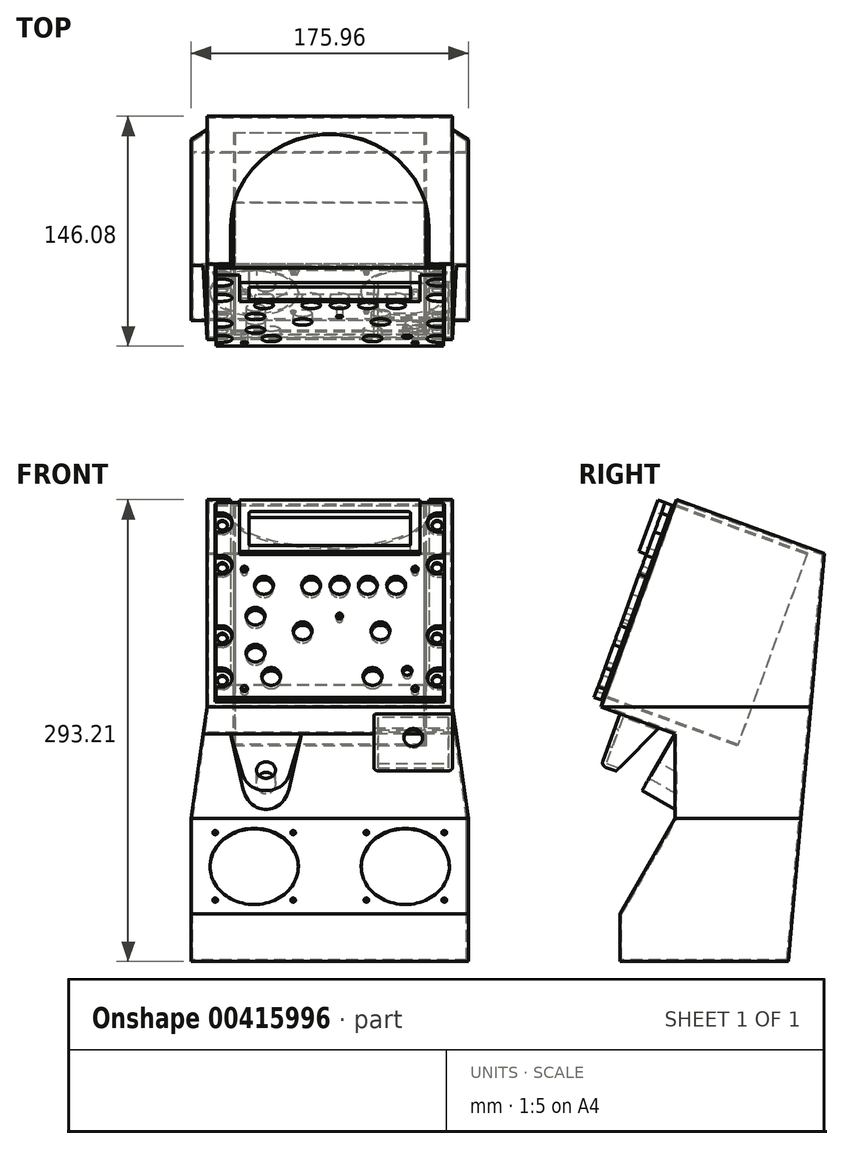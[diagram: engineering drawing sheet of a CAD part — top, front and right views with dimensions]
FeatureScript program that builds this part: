
annotation { "Feature Type Name" : "Feature", "Feature Type Description" : "" }
export const myFeature = defineFeature(function(context is Context, id is Id, definition is map)
    precondition{}
    {
        {
            var Q0;
            Q0=qCreatedBy(makeId("Right.planeOp"),FACE);
            var sketch = newSketch(context, id + "F0", { "sketchPlane" : qUnion([Q0])});
            skLineSegment(sketch, "E0", {"start": v(0, 0) * mm, "end": v(-47.88, -131.56) * mm});
            skLineSegment(sketch, "E1", {"start": v(-47.88, -131.56) * mm, "end": v(-0.9, -148.66) * mm});
            skLineSegment(sketch, "E2", {"start": v(-0.9, -148.66) * mm, "end": v(-0.9, -202.6) * mm});
            skLineSegment(sketch, "E3", {"start": v(-0.9, -202.6) * mm, "end": v(-35.9, -263.21) * mm});
            skLineSegment(sketch, "E4", {"start": v(-35.9, -263.21) * mm, "end": v(-35.9, -293.21) * mm});
            skLineSegment(sketch, "E5", {"start": v(-35.9, -293.21) * mm, "end": v(71.3, -293.21) * mm});
            skLineSegment(sketch, "E6", {"start": v(71.3, -293.21) * mm, "end": v(93.97, -34.2) * mm});
            skLineSegment(sketch, "E7", {"start": v(93.97, -34.2) * mm, "end": v(0, 0) * mm});
            skSolve(sketch);
        }
        {
            var Q0;
            Q0=qSketchRegion(id+"F0",true);
            extrude(context, id + "F1", {"entities" : qUnion([Q0]), "depth" : 200 * mm});
        }
        {
            var Q0;
            Q0=makeQuery(id+"F1.opExtrude","SWEPT_FACE",FACE,{"disambiguationData":[OSD([sQuery(id+"F0.wireOp",EDGE,"E2")])]});
            var sketch = newSketch(context, id + "F2", { "sketchPlane" : qUnion([Q0])});
            skLineSegment(sketch, "E8", {"start": v(178, 0) * mm, "end": v(178, -131.56) * mm});
            skLineSegment(sketch, "E9", {"start": v(178, -131.56) * mm, "end": v(187.98, -202.6) * mm});
            skLineSegment(sketch, "E10", {"start": v(187.98, -202.6) * mm, "end": v(187.98, -293.21) * mm});
            skLineSegment(sketch, "E11", {"start": v(187.98, -293.21) * mm, "end": v(228, -293.21) * mm});
            skLineSegment(sketch, "E12", {"start": v(228, -293.21) * mm, "end": v(228, 0) * mm});
            skLineSegment(sketch, "E13", {"start": v(228, 0) * mm, "end": v(178, 0) * mm});
            skLineSegment(sketch, "E14", {"start": v(0, 0) * mm, "end": v(22, 0) * mm});
            skLineSegment(sketch, "E15", {"start": v(22, 0) * mm, "end": v(22, -131.56) * mm});
            skLineSegment(sketch, "E16", {"start": v(22, -131.56) * mm, "end": v(12.02, -202.6) * mm});
            skLineSegment(sketch, "E17", {"start": v(12.02, -202.6) * mm, "end": v(12.02, -293.21) * mm});
            skLineSegment(sketch, "E18", {"start": v(12.02, -293.21) * mm, "end": v(-28, -293.21) * mm});
            skLineSegment(sketch, "E19", {"start": v(-28, -293.21) * mm, "end": v(-28, 0) * mm});
            skLineSegment(sketch, "E20", {"start": v(-28, 0) * mm, "end": v(22, 0) * mm});
            skLineSegment(sketch, "E21", {"start": v(22, -35.34) * mm, "end": v(0, -35.34) * mm, "construction": true});
            skLineSegment(sketch, "E22", {"start": v(178, -36.32) * mm, "end": v(200, -36.32) * mm, "construction": true});
            skSolve(sketch);
        }
        {
            var Q0;
            Q0=qSketchRegion(id+"F2",true);
            var Q1;
            Q1=makeQuery(id+"F1.opExtrude","SWEPT_FACE",FACE,{"disambiguationData":[OSD([sQuery(id+"F0.wireOp",EDGE,"E6")])]});
            extrude(context, id + "F3", {"entities" : qUnion([Q0]), "operationType" : NewBodyOperationType.REMOVE, "endBound" : BoundingType.UP_TO_SURFACE, "oppositeDirection" : true, "endBoundEntityFace" : qUnion([Q1]), "depth" : 25 * mm, "hasSecondDirection" : true, "secondDirectionOppositeDirection" : false, "secondDirectionDepth" : 150 * mm});
        }
        {
            var Q0;
            Q0=makeQuery(id+"F1.opExtrude","SWEPT_FACE",FACE,{"disambiguationData":[OSD([sQuery(id+"F0.wireOp",EDGE,"E0")])]});
            var sketch = newSketch(context, id + "F4", { "sketchPlane" : qUnion([Q0])});
            skLineSegment(sketch, "E23.bottom", {"start": v(37, -1) * mm, "end": v(163, -1) * mm});
            skLineSegment(sketch, "E23.top", {"start": v(37, -125) * mm, "end": v(163, -125) * mm});
            skLineSegment(sketch, "E23.left", {"start": v(37, -1) * mm, "end": v(37, -125) * mm});
            skLineSegment(sketch, "E23.right", {"start": v(163, -1) * mm, "end": v(163, -125) * mm});
            skSolve(sketch);
        }
        {
            var Q0;
            Q0=qSketchRegion(id+"F4",true);
            extrude(context, id + "F5", {"entities" : qUnion([Q0]), "operationType" : NewBodyOperationType.REMOVE, "oppositeDirection" : true, "depth" : 1 * mm});
        }
        {
            var Q0;
            Q0=makeQuery(id+"F5.boolean.opBoolean","COPY",FACE,{"derivedFrom":makeQuery(id+"F5.opExtrude","CAP_FACE",FACE,{"disambiguationData":[OSD([sQuery(id+"F4.wireOp",EDGE,"E23.bottom"),sQuery(id+"F4.wireOp",EDGE,"E23.top"),sQuery(id+"F4.wireOp",EDGE,"E23.left"),sQuery(id+"F4.wireOp",EDGE,"E23.right")])],"isStart":false})});
            shell(context, id + "F6", {"entities" : qUnion([Q0]), "thickness" : 1 * mm});
        }
        {
            var Q0;
            Q0=makeQuery(id+"F1.opExtrude","SWEPT_FACE",FACE,{"disambiguationData":[OSD([sQuery(id+"F0.wireOp",EDGE,"E7")])]});
            var sketch = newSketch(context, id + "F7", { "sketchPlane" : qUnion([Q0])});
            skLineSegment(sketch, "E24", {"start": v(37, 0) * mm, "end": v(37, 25) * mm});
            skLineSegment(sketch, "E25", {"start": v(163, 0) * mm, "end": v(163, 25) * mm});
            skArc(sketch, "E26", {"start": v(163, 25) * mm, "mid": v(100, 88) * mm, "end": v(37, 25) * mm});
            skLineSegment(sketch, "E27", {"start": v(37, 0) * mm, "end": v(163, 0) * mm});
            skSolve(sketch);
        }
        {
            var Q0;
            Q0=qSketchRegion(id+"F7",true);
            extrude(context, id + "F8", {"entities" : qUnion([Q0]), "operationType" : NewBodyOperationType.REMOVE, "endBound" : BoundingType.UP_TO_NEXT, "oppositeDirection" : true, "depth" : 25 * mm});
        }
        {
            var Q0;
            Q0=makeQuery(id+"F1.opExtrude","SWEPT_FACE",FACE,{"disambiguationData":[OSD([sQuery(id+"F0.wireOp",EDGE,"E3")])]});
            var sketch = newSketch(context, id + "F9", { "sketchPlane" : qUnion([Q0])});
            skCircle(sketch, "E28", {"center": v(52.02, -210.9) * mm, "radius": 28 * mm});
            skCircle(sketch, "E29", {"center": v(147.98, -210.9) * mm, "radius": 28 * mm});
            skLineSegment(sketch, "E30", {"start": v(52.02, -210.9) * mm, "end": v(52.02, -175.9) * mm, "construction": true});
            skLineSegment(sketch, "E31", {"start": v(52.02, -210.9) * mm, "end": v(52.02, -245.9) * mm, "construction": true});
            skSolve(sketch);
        }
        {
            var Q0;
            Q0=qSketchRegion(id+"F9",true);
            extrude(context, id + "F10", {"entities" : qUnion([Q0]), "operationType" : NewBodyOperationType.REMOVE, "endBound" : BoundingType.UP_TO_NEXT, "oppositeDirection" : true, "depth" : 25 * mm});
        }
        {
            var Q0;
            Q0=makeQuery(id+"F3.boolean.opBoolean","COPY",FACE,{"derivedFrom":makeQuery(id+"F3.opExtrude","SWEPT_FACE",FACE,{"disambiguationData":[OSD([sQuery(id+"F2.wireOp",EDGE,"E8")])]})});
            var sketch = newSketch(context, id + "F11", { "sketchPlane" : qUnion([Q0])});
            skLineSegment(sketch, "E32", {"start": v(-35.67, -136) * mm, "end": v(-47.64, -168.9) * mm});
            skLineSegment(sketch, "E33", {"start": v(-47.64, -168.9) * mm, "end": v(-38.24, -172.31) * mm});
            skLineSegment(sketch, "E34", {"start": v(-38.24, -172.31) * mm, "end": v(-10.93, -145) * mm});
            skLineSegment(sketch, "E35", {"start": v(-10.93, -145) * mm, "end": v(-35.67, -136) * mm});
            skSolve(sketch);
        }
        {
            var Q0;
            Q0=qSketchRegion(id+"F11",true);
            extrude(context, id + "F12", {"entities" : qUnion([Q0]), "operationType" : NewBodyOperationType.ADD, "oppositeDirection" : true, "depth" : 50 * mm});
        }
        {
            var Q0;
            Q0=makeQuery(id+"F12.opExtrude","SWEPT_FACE",FACE,{"disambiguationData":[OSD([sQuery(id+"F11.wireOp",EDGE,"E34")])]});
            shell(context, id + "F13", {"entities" : qUnion([Q0]), "thickness" : 2.5 * mm});
        }
        {
            var Q0;
            Q0=makeQuery(id+"F12.opExtrude","CAP_EDGE",EDGE,{"disambiguationData":[OSD([sQuery(id+"F11.wireOp",EDGE,"E32")])],"isStart":false});
            var Q1;
            Q1=makeQuery(id+"F12.opExtrude","SWEPT_EDGE",EDGE,{"disambiguationData":[OSD([sQuery(id+"F11.wireOp",EDGE,"E32"),sQuery(id+"F11.wireOp",EDGE,"E33")])]});
            var Q2;
            Q2=makeQuery(id+"F12.opExtrude","CAP_EDGE",EDGE,{"disambiguationData":[OSD([sQuery(id+"F11.wireOp",EDGE,"E32")])],"isStart":true});
            var Q3;
            Q3=makeQuery(id+"F12.opExtrude","CAP_EDGE",EDGE,{"disambiguationData":[OSD([sQuery(id+"F11.wireOp",EDGE,"E33")])],"isStart":false});
            var Q4;
            Q4=makeQuery(id+"F12.opExtrude","CAP_EDGE",EDGE,{"disambiguationData":[OSD([sQuery(id+"F11.wireOp",EDGE,"E33")])],"isStart":true});
            fillet(context, id + "F14", {"entities" : qUnion([Q0, Q1, Q2, Q3, Q4]), "radius" : 3 * mm, "tangentPropagation" : true, "allowEdgeOverflow" : false});
        }
        {
            var Q0;
            Q0=makeQuery(id+"F1.opExtrude","SWEPT_EDGE",EDGE,{"disambiguationData":[OSD([sQuery(id+"F0.wireOp",EDGE,"E1"),sQuery(id+"F0.wireOp",EDGE,"E2")])]});
            cPlane(context, id + "F15", {"entities" : qUnion([Q0]), "cplaneType" : CPlaneType.LINE_ANGLE, "offset" : 25 * mm, "angle" : 30 * degree, "width" : 150 * mm, "height" : 150 * mm});
        }
        {
            var Q0;
            Q0=qCreatedBy(id+"F15.planeOp",FACE);
            var sketch = newSketch(context, id + "F16", { "sketchPlane" : qUnion([Q0])});
            skLineSegment(sketch, "E36", {"start": v(37, -129.2) * mm, "end": v(44.99, -159.7) * mm});
            skLineSegment(sketch, "E37", {"start": v(82, -129.2) * mm, "end": v(74.01, -159.7) * mm});
            skArc(sketch, "E38", {"start": v(44.99, -159.7) * mm, "mid": v(59.5, -170.9) * mm, "end": v(74.01, -159.7) * mm});
            skLineSegment(sketch, "E39", {"start": v(37, -129.2) * mm, "end": v(82, -129.2) * mm});
            skSolve(sketch);
        }
        {
            var Q0;
            Q0=qSketchRegion(id+"F16",true);
            var Q1;
            Q1=makeQuery(id+"F1.opExtrude","SWEPT_FACE",FACE,{"disambiguationData":[OSD([sQuery(id+"F0.wireOp",EDGE,"E2")])]});
            extrude(context, id + "F17", {"entities" : qUnion([Q0]), "operationType" : NewBodyOperationType.ADD, "endBound" : BoundingType.UP_TO_SURFACE, "oppositeDirection" : true, "endBoundEntityFace" : qUnion([Q1]), "depth" : 25 * mm});
        }
        {
            var Q0;
            Q0=makeQuery(id+"F17.opExtrude","CAP_FACE",FACE,{"disambiguationData":[OSD([sQuery(id+"F16.wireOp",EDGE,"E36"),sQuery(id+"F16.wireOp",EDGE,"E37"),sQuery(id+"F16.wireOp",EDGE,"E38"),sQuery(id+"F16.wireOp",EDGE,"E39")])],"isStart":true});
            var sketch = newSketch(context, id + "F18", { "sketchPlane" : qUnion([Q0])});
            skCircle(sketch, "E40", {"center": v(59.5, -155.9) * mm, "radius": 6 * mm});
            skSolve(sketch);
        }
        {
            var Q0;
            Q0=qSketchRegion(id+"F18",true);
            extrude(context, id + "F19", {"entities" : qUnion([Q0]), "operationType" : NewBodyOperationType.REMOVE, "endBound" : BoundingType.UP_TO_NEXT, "oppositeDirection" : true, "depth" : 25 * mm});
        }
        {
            var Q0;
            Q0=makeQuery(id+"F12.opExtrude","SWEPT_FACE",FACE,{"disambiguationData":[OSD([sQuery(id+"F11.wireOp",EDGE,"E32")])]});
            var sketch = newSketch(context, id + "F20", { "sketchPlane" : qUnion([Q0])});
            skCircle(sketch, "E41", {"center": v(153, -156) * mm, "radius": 6 * mm});
            skLineSegment(sketch, "E42", {"start": v(153, -156) * mm, "end": v(153, -140) * mm, "construction": true});
            skLineSegment(sketch, "E43", {"start": v(153, -156) * mm, "end": v(153, -172) * mm, "construction": true});
            skLineSegment(sketch, "E44", {"start": v(153, -156) * mm, "end": v(131, -156) * mm, "construction": true});
            skLineSegment(sketch, "E45", {"start": v(153, -156) * mm, "end": v(175, -156) * mm, "construction": true});
            skSolve(sketch);
        }
        {
            var Q0;
            Q0=qSketchRegion(id+"F20",true);
            extrude(context, id + "F21", {"entities" : qUnion([Q0]), "operationType" : NewBodyOperationType.REMOVE, "oppositeDirection" : true, "depth" : 5 * mm});
        }
        {
            var Q0;
            Q0=makeQuery(id+"F1.opExtrude","SWEPT_FACE",FACE,{"disambiguationData":[OSD([sQuery(id+"F0.wireOp",EDGE,"E0")])]});
            var sketch = newSketch(context, id + "F22", { "sketchPlane" : qUnion([Q0])});
            skLineSegment(sketch, "E46.bottom", {"start": v(27, -3.33) * mm, "end": v(173, -3.33) * mm});
            skLineSegment(sketch, "E46.top", {"start": v(27, -136.68) * mm, "end": v(173, -136.68) * mm});
            skLineSegment(sketch, "E46.left", {"start": v(27, -3.33) * mm, "end": v(27, -136.68) * mm});
            skLineSegment(sketch, "E46.right", {"start": v(173, -3.33) * mm, "end": v(173, -136.68) * mm});
            skLineSegment(sketch, "E47", {"start": v(27, -136.68) * mm, "end": v(22, -136.68) * mm, "construction": true});
            skLineSegment(sketch, "E48", {"start": v(173, -136.68) * mm, "end": v(178, -136.68) * mm, "construction": true});
            skLineSegment(sketch, "E49", {"start": v(27, -136.68) * mm, "end": v(27, -140) * mm, "construction": true});
            skLineSegment(sketch, "E50", {"start": v(27, -3.33) * mm, "end": v(27, 0) * mm, "construction": true});
            skSolve(sketch);
        }
        {
            var Q0;
            Q0=qSketchRegion(id+"F22",true);
            extrude(context, id + "F23", {"entities" : qUnion([Q0]), "depth" : 1 * mm});
        }
        {
            var Q0;
            Q0=makeQuery(id+"F23.opExtrude","CAP_FACE",FACE,{"disambiguationData":[OSD([sQuery(id+"F22.wireOp",EDGE,"E46.bottom"),sQuery(id+"F22.wireOp",EDGE,"E46.top"),sQuery(id+"F22.wireOp",EDGE,"E46.left"),sQuery(id+"F22.wireOp",EDGE,"E46.right")])],"isStart":false});
            var sketch = newSketch(context, id + "F24", { "sketchPlane" : qUnion([Q0])});
            skLineSegment(sketch, "E51.bottom", {"start": v(27.8, -4.13) * mm, "end": v(172.2, -4.13) * mm});
            skLineSegment(sketch, "E51.top", {"start": v(27.8, -135.88) * mm, "end": v(172.2, -135.88) * mm});
            skLineSegment(sketch, "E51.left", {"start": v(27.8, -4.13) * mm, "end": v(27.8, -11.26) * mm});
            skLineSegment(sketch, "E51.right", {"start": v(172.2, -4.13) * mm, "end": v(172.2, -11.26) * mm});
            skArc(sketch, "E52", {"start": v(168.24, -11.26) * mm, "mid": v(161.89, -17.61) * mm, "end": v(168.24, -23.96) * mm});
            skArc(sketch, "E53", {"start": v(168.24, -39.84) * mm, "mid": v(161.89, -46.19) * mm, "end": v(168.24, -52.54) * mm});
            skArc(sketch, "E54", {"start": v(168.24, -87.46) * mm, "mid": v(161.89, -93.81) * mm, "end": v(168.24, -100.16) * mm});
            skArc(sketch, "E55", {"start": v(168.24, -116.04) * mm, "mid": v(161.89, -122.39) * mm, "end": v(168.24, -128.74) * mm});
            skArc(sketch, "E56", {"start": v(31.76, -23.96) * mm, "mid": v(38.11, -17.61) * mm, "end": v(31.76, -11.26) * mm});
            skArc(sketch, "E57", {"start": v(31.76, -52.54) * mm, "mid": v(38.11, -46.19) * mm, "end": v(31.76, -39.84) * mm});
            skArc(sketch, "E58", {"start": v(31.76, -100.16) * mm, "mid": v(38.11, -93.81) * mm, "end": v(31.76, -87.46) * mm});
            skArc(sketch, "E59", {"start": v(31.76, -128.74) * mm, "mid": v(38.11, -122.39) * mm, "end": v(31.76, -116.04) * mm});
            skLineSegment(sketch, "E60", {"start": v(31.76, -11.26) * mm, "end": v(27.8, -11.26) * mm});
            skLineSegment(sketch, "E61", {"start": v(31.76, -23.96) * mm, "end": v(27.8, -23.96) * mm});
            skLineSegment(sketch, "E62", {"start": v(31.76, -39.84) * mm, "end": v(27.8, -39.84) * mm});
            skLineSegment(sketch, "E63", {"start": v(31.76, -52.54) * mm, "end": v(27.8, -52.54) * mm});
            skLineSegment(sketch, "E64", {"start": v(168.24, -11.26) * mm, "end": v(172.2, -11.26) * mm});
            skLineSegment(sketch, "E65", {"start": v(168.24, -23.96) * mm, "end": v(172.2, -23.96) * mm});
            skLineSegment(sketch, "E66", {"start": v(168.24, -39.84) * mm, "end": v(172.2, -39.84) * mm});
            skLineSegment(sketch, "E67", {"start": v(168.24, -52.54) * mm, "end": v(172.2, -52.54) * mm});
            skLineSegment(sketch, "E68", {"start": v(31.76, -87.46) * mm, "end": v(27.8, -87.46) * mm});
            skLineSegment(sketch, "E69", {"start": v(31.76, -100.16) * mm, "end": v(27.8, -100.16) * mm});
            skLineSegment(sketch, "E70", {"start": v(31.76, -116.04) * mm, "end": v(27.8, -116.04) * mm});
            skLineSegment(sketch, "E71", {"start": v(31.76, -128.74) * mm, "end": v(27.8, -128.74) * mm});
            skLineSegment(sketch, "E72", {"start": v(168.24, -87.46) * mm, "end": v(172.2, -87.46) * mm});
            skLineSegment(sketch, "E73", {"start": v(168.24, -100.16) * mm, "end": v(172.2, -100.16) * mm});
            skLineSegment(sketch, "E74", {"start": v(168.24, -116.04) * mm, "end": v(172.2, -116.04) * mm});
            skLineSegment(sketch, "E75", {"start": v(168.24, -128.74) * mm, "end": v(172.2, -128.74) * mm});
            skLineSegment(sketch, "E76.trimOffspring", {"start": v(27.8, -23.96) * mm, "end": v(27.8, -39.84) * mm});
            skLineSegment(sketch, "E77.trimOffspring", {"start": v(27.8, -52.54) * mm, "end": v(27.8, -87.46) * mm});
            skLineSegment(sketch, "E78.trimOffspring", {"start": v(27.8, -100.16) * mm, "end": v(27.8, -116.04) * mm});
            skLineSegment(sketch, "E79.trimOffspring", {"start": v(27.8, -128.74) * mm, "end": v(27.8, -135.88) * mm});
            skLineSegment(sketch, "E80.trimOffspring", {"start": v(172.2, -23.96) * mm, "end": v(172.2, -39.84) * mm});
            skLineSegment(sketch, "E81.trimOffspring", {"start": v(172.2, -52.54) * mm, "end": v(172.2, -87.46) * mm});
            skLineSegment(sketch, "E82.trimOffspring", {"start": v(172.2, -100.16) * mm, "end": v(172.2, -116.04) * mm});
            skLineSegment(sketch, "E83.trimOffspring", {"start": v(172.2, -128.74) * mm, "end": v(172.2, -135.88) * mm});
            skSolve(sketch);
        }
        {
            var Q0;
            Q0=qSketchRegion(id+"F24",true);
            extrude(context, id + "F25", {"entities" : qUnion([Q0]), "operationType" : NewBodyOperationType.ADD, "depth" : 5 * mm});
        }
        {
            var Q0;
            Q0=makeQuery(id+"F23.opExtrude","CAP_FACE",FACE,{"disambiguationData":[OSD([sQuery(id+"F22.wireOp",EDGE,"E46.bottom"),sQuery(id+"F22.wireOp",EDGE,"E46.top"),sQuery(id+"F22.wireOp",EDGE,"E46.left"),sQuery(id+"F22.wireOp",EDGE,"E46.right")])],"isStart":false});
            var sketch = newSketch(context, id + "F26", { "sketchPlane" : qUnion([Q0])});
            skCircle(sketch, "E84", {"center": v(31.76, -17.61) * mm, "radius": 3.24 * mm});
            skCircle(sketch, "E85", {"center": v(168.24, -17.61) * mm, "radius": 3.24 * mm});
            skCircle(sketch, "E86", {"center": v(168.24, -46.19) * mm, "radius": 3.24 * mm});
            skCircle(sketch, "E87", {"center": v(31.76, -46.19) * mm, "radius": 3.24 * mm});
            skCircle(sketch, "E88", {"center": v(31.76, -93.81) * mm, "radius": 3.24 * mm});
            skCircle(sketch, "E89", {"center": v(31.76, -122.39) * mm, "radius": 3.24 * mm});
            skCircle(sketch, "E90", {"center": v(168.24, -93.81) * mm, "radius": 3.24 * mm});
            skCircle(sketch, "E91", {"center": v(168.24, -122.39) * mm, "radius": 3.24 * mm});
            skSolve(sketch);
        }
        {
            var Q0;
            Q0=qSketchRegion(id+"F26",true);
            var Q1;
            Q1=makeQuery(id+"F6.opShell","OFFSET_FACE",FACE,{"disambiguationData":[OSD([sQuery(id+"F0.wireOp",EDGE,"E0"),sQuery(id+"F4.wireOp",EDGE,"E23.bottom"),sQuery(id+"F4.wireOp",EDGE,"E23.top"),sQuery(id+"F4.wireOp",EDGE,"E23.left"),sQuery(id+"F4.wireOp",EDGE,"E23.right")])]});
            extrude(context, id + "F27", {"entities" : qUnion([Q0]), "operationType" : NewBodyOperationType.REMOVE, "endBound" : BoundingType.UP_TO_SURFACE, "oppositeDirection" : true, "endBoundEntityFace" : qUnion([Q1]), "depth" : 25 * mm});
        }
        {
            var Q0;
            Q0=makeQuery(id+"F23.opExtrude","CAP_FACE",FACE,{"disambiguationData":[OSD([sQuery(id+"F22.wireOp",EDGE,"E46.bottom"),sQuery(id+"F22.wireOp",EDGE,"E46.top"),sQuery(id+"F22.wireOp",EDGE,"E46.left"),sQuery(id+"F22.wireOp",EDGE,"E46.right")])],"isStart":true});
            var sketch = newSketch(context, id + "F28", { "sketchPlane" : qUnion([Q0])});
            skLineSegment(sketch, "E92.bottom", {"start": v(-161, -3.33) * mm, "end": v(-39, -3.33) * mm});
            skLineSegment(sketch, "E92.top", {"start": v(-161, -133.68) * mm, "end": v(-39, -133.68) * mm});
            skLineSegment(sketch, "E92.left", {"start": v(-161, -3.33) * mm, "end": v(-161, -133.68) * mm});
            skLineSegment(sketch, "E92.right", {"start": v(-39, -3.33) * mm, "end": v(-39, -133.67) * mm});
            skLineSegment(sketch, "E93.bottom", {"start": v(-160, -4.33) * mm, "end": v(-40, -4.33) * mm});
            skLineSegment(sketch, "E93.top", {"start": v(-160, -132.68) * mm, "end": v(-40, -132.68) * mm});
            skLineSegment(sketch, "E93.left", {"start": v(-160, -4.33) * mm, "end": v(-160, -132.68) * mm});
            skLineSegment(sketch, "E93.right", {"start": v(-40, -4.33) * mm, "end": v(-40, -132.68) * mm});
            skSolve(sketch);
        }
        {
            var Q0;
            Q0=qSketchRegion(id+"F28",true);
            extrude(context, id + "F29", {"entities" : qUnion([Q0]), "operationType" : NewBodyOperationType.ADD, "depth" : 90 * mm});
        }
        {
            var Q0;
            Q0=makeQuery(id+"F25.opExtrude","CAP_FACE",FACE,{"disambiguationData":[OSD([sQuery(id+"F24.wireOp",EDGE,"E51.bottom"),sQuery(id+"F24.wireOp",EDGE,"E51.top"),sQuery(id+"F24.wireOp",EDGE,"E51.left"),sQuery(id+"F24.wireOp",EDGE,"E51.right"),sQuery(id+"F24.wireOp",EDGE,"E52"),sQuery(id+"F24.wireOp",EDGE,"E53"),sQuery(id+"F24.wireOp",EDGE,"E54"),sQuery(id+"F24.wireOp",EDGE,"E55"),sQuery(id+"F24.wireOp",EDGE,"E56"),sQuery(id+"F24.wireOp",EDGE,"E57"),sQuery(id+"F24.wireOp",EDGE,"E58"),sQuery(id+"F24.wireOp",EDGE,"E59"),sQuery(id+"F24.wireOp",EDGE,"E60"),sQuery(id+"F24.wireOp",EDGE,"E61"),sQuery(id+"F24.wireOp",EDGE,"E62"),sQuery(id+"F24.wireOp",EDGE,"E63"),sQuery(id+"F24.wireOp",EDGE,"E64"),sQuery(id+"F24.wireOp",EDGE,"E65"),sQuery(id+"F24.wireOp",EDGE,"E66"),sQuery(id+"F24.wireOp",EDGE,"E67"),sQuery(id+"F24.wireOp",EDGE,"E68"),sQuery(id+"F24.wireOp",EDGE,"E69"),sQuery(id+"F24.wireOp",EDGE,"E70"),sQuery(id+"F24.wireOp",EDGE,"E71"),sQuery(id+"F24.wireOp",EDGE,"E72"),sQuery(id+"F24.wireOp",EDGE,"E73"),sQuery(id+"F24.wireOp",EDGE,"E74"),sQuery(id+"F24.wireOp",EDGE,"E75"),sQuery(id+"F24.wireOp",EDGE,"E76.trimOffspring"),sQuery(id+"F24.wireOp",EDGE,"E77.trimOffspring"),sQuery(id+"F24.wireOp",EDGE,"E78.trimOffspring"),sQuery(id+"F24.wireOp",EDGE,"E79.trimOffspring"),sQuery(id+"F24.wireOp",EDGE,"E80.trimOffspring"),sQuery(id+"F24.wireOp",EDGE,"E81.trimOffspring"),sQuery(id+"F24.wireOp",EDGE,"E82.trimOffspring"),sQuery(id+"F24.wireOp",EDGE,"E83.trimOffspring")])],"isStart":false});
            var sketch = newSketch(context, id + "F30", { "sketchPlane" : qUnion([Q0])});
            skCircle(sketch, "E94", {"center": v(154.2, -49.13) * mm, "radius": 2 * mm});
            skCircle(sketch, "E95", {"center": v(45.8, -49.13) * mm, "radius": 2 * mm});
            skCircle(sketch, "E96", {"center": v(45.8, -129.88) * mm, "radius": 2 * mm});
            skCircle(sketch, "E97", {"center": v(154.2, -129.88) * mm, "radius": 2 * mm});
            skCircle(sketch, "E98", {"center": v(142.2, -60.13) * mm, "radius": 6 * mm});
            skCircle(sketch, "E99.1.0.0", {"center": v(124.2, -60.12) * mm, "radius": 6 * mm});
            skCircle(sketch, "E99.2.0.0", {"center": v(106.2, -60.13) * mm, "radius": 6 * mm});
            skCircle(sketch, "E99.3.0.0", {"center": v(88.2, -60.13) * mm, "radius": 6 * mm});
            skLineSegment(sketch, "E99.direction1", {"start": v(142.2, -60.13) * mm, "end": v(124.2, -60.13) * mm, "construction": true});
            skCircle(sketch, "E100", {"center": v(58.2, -60.13) * mm, "radius": 6 * mm});
            skCircle(sketch, "E101", {"center": v(132.2, -90.88) * mm, "radius": 6 * mm});
            skCircle(sketch, "E102", {"center": v(82.8, -90.88) * mm, "radius": 6 * mm});
            skCircle(sketch, "E103", {"center": v(52.8, -80.88) * mm, "radius": 6 * mm});
            skCircle(sketch, "E104", {"center": v(52.8, -105.88) * mm, "radius": 6 * mm});
            skCircle(sketch, "E105", {"center": v(62.8, -121.68) * mm, "radius": 6 * mm});
            skCircle(sketch, "E106", {"center": v(127.2, -121.68) * mm, "radius": 6 * mm});
            skCircle(sketch, "E107", {"center": v(149.2, -117.88) * mm, "radius": 3 * mm});
            skCircle(sketch, "E108", {"center": v(106.2, -80.88) * mm, "radius": 2 * mm});
            skSolve(sketch);
        }
        {
            var Q0;
            Q0=qSketchRegion(id+"F30",true);
            extrude(context, id + "F31", {"entities" : qUnion([Q0]), "operationType" : NewBodyOperationType.REMOVE, "endBound" : BoundingType.UP_TO_NEXT, "oppositeDirection" : true, "depth" : 25 * mm});
        }
        {
            var Q0;
            Q0=makeQuery(id+"F1.opExtrude","SWEPT_FACE",FACE,{"disambiguationData":[OSD([sQuery(id+"F0.wireOp",EDGE,"E3")])]});
            var sketch = newSketch(context, id + "F32", { "sketchPlane" : qUnion([Q0])});
            skLineSegment(sketch, "E109", {"start": v(52.02, -210.9) * mm, "end": v(76.77, -186.15) * mm, "construction": true});
            skCircle(sketch, "E110", {"center": v(76.77, -186.15) * mm, "radius": 1.5 * mm});
            skLineSegment(sketch, "E111", {"start": v(52.02, -210.9) * mm, "end": v(27.27, -235.65) * mm, "construction": true});
            skCircle(sketch, "E112", {"center": v(27.27, -235.65) * mm, "radius": 1.5 * mm});
            skCircle(sketch, "E113", {"center": v(76.77, -235.65) * mm, "radius": 1.5 * mm});
            skCircle(sketch, "E114", {"center": v(27.27, -186.15) * mm, "radius": 1.5 * mm});
            skLineSegment(sketch, "E115", {"start": v(147.98, -210.9) * mm, "end": v(123.23, -186.15) * mm, "construction": true});
            skCircle(sketch, "E116", {"center": v(123.23, -186.15) * mm, "radius": 1.5 * mm});
            skCircle(sketch, "E117", {"center": v(123.23, -235.65) * mm, "radius": 1.5 * mm});
            skLineSegment(sketch, "E118", {"start": v(147.98, -210.9) * mm, "end": v(172.73, -235.65) * mm, "construction": true});
            skCircle(sketch, "E119", {"center": v(172.73, -235.65) * mm, "radius": 1.5 * mm});
            skCircle(sketch, "E120", {"center": v(172.73, -186.15) * mm, "radius": 1.5 * mm});
            skSolve(sketch);
        }
        {
            var Q0;
            Q0=qSketchRegion(id+"F32",true);
            extrude(context, id + "F33", {"entities" : qUnion([Q0]), "operationType" : NewBodyOperationType.REMOVE, "endBound" : BoundingType.UP_TO_NEXT, "oppositeDirection" : true, "depth" : 25 * mm});
        }
        {
            var Q0;
            Q0=makeQuery(id+"F25.opExtrude","CAP_FACE",FACE,{"disambiguationData":[OSD([sQuery(id+"F24.wireOp",EDGE,"E51.bottom"),sQuery(id+"F24.wireOp",EDGE,"E51.top"),sQuery(id+"F24.wireOp",EDGE,"E51.left"),sQuery(id+"F24.wireOp",EDGE,"E51.right"),sQuery(id+"F24.wireOp",EDGE,"E52"),sQuery(id+"F24.wireOp",EDGE,"E53"),sQuery(id+"F24.wireOp",EDGE,"E54"),sQuery(id+"F24.wireOp",EDGE,"E55"),sQuery(id+"F24.wireOp",EDGE,"E56"),sQuery(id+"F24.wireOp",EDGE,"E57"),sQuery(id+"F24.wireOp",EDGE,"E58"),sQuery(id+"F24.wireOp",EDGE,"E59"),sQuery(id+"F24.wireOp",EDGE,"E60"),sQuery(id+"F24.wireOp",EDGE,"E61"),sQuery(id+"F24.wireOp",EDGE,"E62"),sQuery(id+"F24.wireOp",EDGE,"E63"),sQuery(id+"F24.wireOp",EDGE,"E64"),sQuery(id+"F24.wireOp",EDGE,"E65"),sQuery(id+"F24.wireOp",EDGE,"E66"),sQuery(id+"F24.wireOp",EDGE,"E67"),sQuery(id+"F24.wireOp",EDGE,"E68"),sQuery(id+"F24.wireOp",EDGE,"E69"),sQuery(id+"F24.wireOp",EDGE,"E70"),sQuery(id+"F24.wireOp",EDGE,"E71"),sQuery(id+"F24.wireOp",EDGE,"E72"),sQuery(id+"F24.wireOp",EDGE,"E73"),sQuery(id+"F24.wireOp",EDGE,"E74"),sQuery(id+"F24.wireOp",EDGE,"E75"),sQuery(id+"F24.wireOp",EDGE,"E76.trimOffspring"),sQuery(id+"F24.wireOp",EDGE,"E77.trimOffspring"),sQuery(id+"F24.wireOp",EDGE,"E78.trimOffspring"),sQuery(id+"F24.wireOp",EDGE,"E79.trimOffspring"),sQuery(id+"F24.wireOp",EDGE,"E80.trimOffspring"),sQuery(id+"F24.wireOp",EDGE,"E81.trimOffspring"),sQuery(id+"F24.wireOp",EDGE,"E82.trimOffspring"),sQuery(id+"F24.wireOp",EDGE,"E83.trimOffspring")])],"isStart":false});
            var sketch = newSketch(context, id + "F34", { "sketchPlane" : qUnion([Q0])});
            skLineSegment(sketch, "E121.bottom", {"start": v(42.8, -4.13) * mm, "end": v(157.2, -4.13) * mm});
            skLineSegment(sketch, "E121.top", {"start": v(42.8, -39.13) * mm, "end": v(157.2, -39.13) * mm});
            skLineSegment(sketch, "E121.left", {"start": v(42.8, -4.13) * mm, "end": v(42.8, -39.13) * mm});
            skLineSegment(sketch, "E121.right", {"start": v(157.2, -4.13) * mm, "end": v(157.2, -39.13) * mm});
            skSolve(sketch);
        }
        {
            var Q0;
            Q0=qSketchRegion(id+"F34",true);
            extrude(context, id + "F35", {"entities" : qUnion([Q0]), "operationType" : NewBodyOperationType.ADD, "depth" : 5 * mm});
        }
        {
            var Q0;
            Q0=makeQuery(id+"F35.opExtrude","CAP_FACE",FACE,{"disambiguationData":[OSD([sQuery(id+"F34.wireOp",EDGE,"E121.bottom"),sQuery(id+"F34.wireOp",EDGE,"E121.top"),sQuery(id+"F34.wireOp",EDGE,"E121.left"),sQuery(id+"F34.wireOp",EDGE,"E121.right")])],"isStart":false});
            var sketch = newSketch(context, id + "F36", { "sketchPlane" : qUnion([Q0])});
            skLineSegment(sketch, "E122.bottom", {"start": v(49.8, -12.13) * mm, "end": v(150.2, -12.13) * mm});
            skLineSegment(sketch, "E122.top", {"start": v(49.8, -35.13) * mm, "end": v(150.2, -35.13) * mm});
            skLineSegment(sketch, "E122.left", {"start": v(48.8, -13.13) * mm, "end": v(48.8, -34.13) * mm});
            skLineSegment(sketch, "E122.right", {"start": v(151.2, -13.13) * mm, "end": v(151.2, -34.13) * mm});
            skPoint(sketch, "E123.visualSharp", {"position": v(48.8, -12.13) * mm});
            skArc(sketch, "E123.filletArc", {"start": v(49.8, -12.13) * mm, "mid": v(49.1, -12.42) * mm, "end": v(48.8, -13.13) * mm});
            skPoint(sketch, "E124.visualSharp", {"position": v(151.2, -12.13) * mm});
            skArc(sketch, "E124.filletArc", {"start": v(151.2, -13.13) * mm, "mid": v(150.9, -12.42) * mm, "end": v(150.2, -12.13) * mm});
            skPoint(sketch, "E125.visualSharp", {"position": v(151.2, -35.13) * mm});
            skArc(sketch, "E125.filletArc", {"start": v(150.2, -35.13) * mm, "mid": v(150.9, -34.83) * mm, "end": v(151.2, -34.13) * mm});
            skPoint(sketch, "E126.visualSharp", {"position": v(48.8, -35.13) * mm});
            skArc(sketch, "E126.filletArc", {"start": v(48.8, -34.13) * mm, "mid": v(49.1, -34.83) * mm, "end": v(49.8, -35.13) * mm});
            skSolve(sketch);
        }
        {
            var Q0;
            Q0=qSketchRegion(id+"F36",true);
            extrude(context, id + "F37", {"entities" : qUnion([Q0]), "operationType" : NewBodyOperationType.REMOVE, "endBound" : BoundingType.UP_TO_NEXT, "oppositeDirection" : true, "depth" : 25 * mm});
        }
    });
